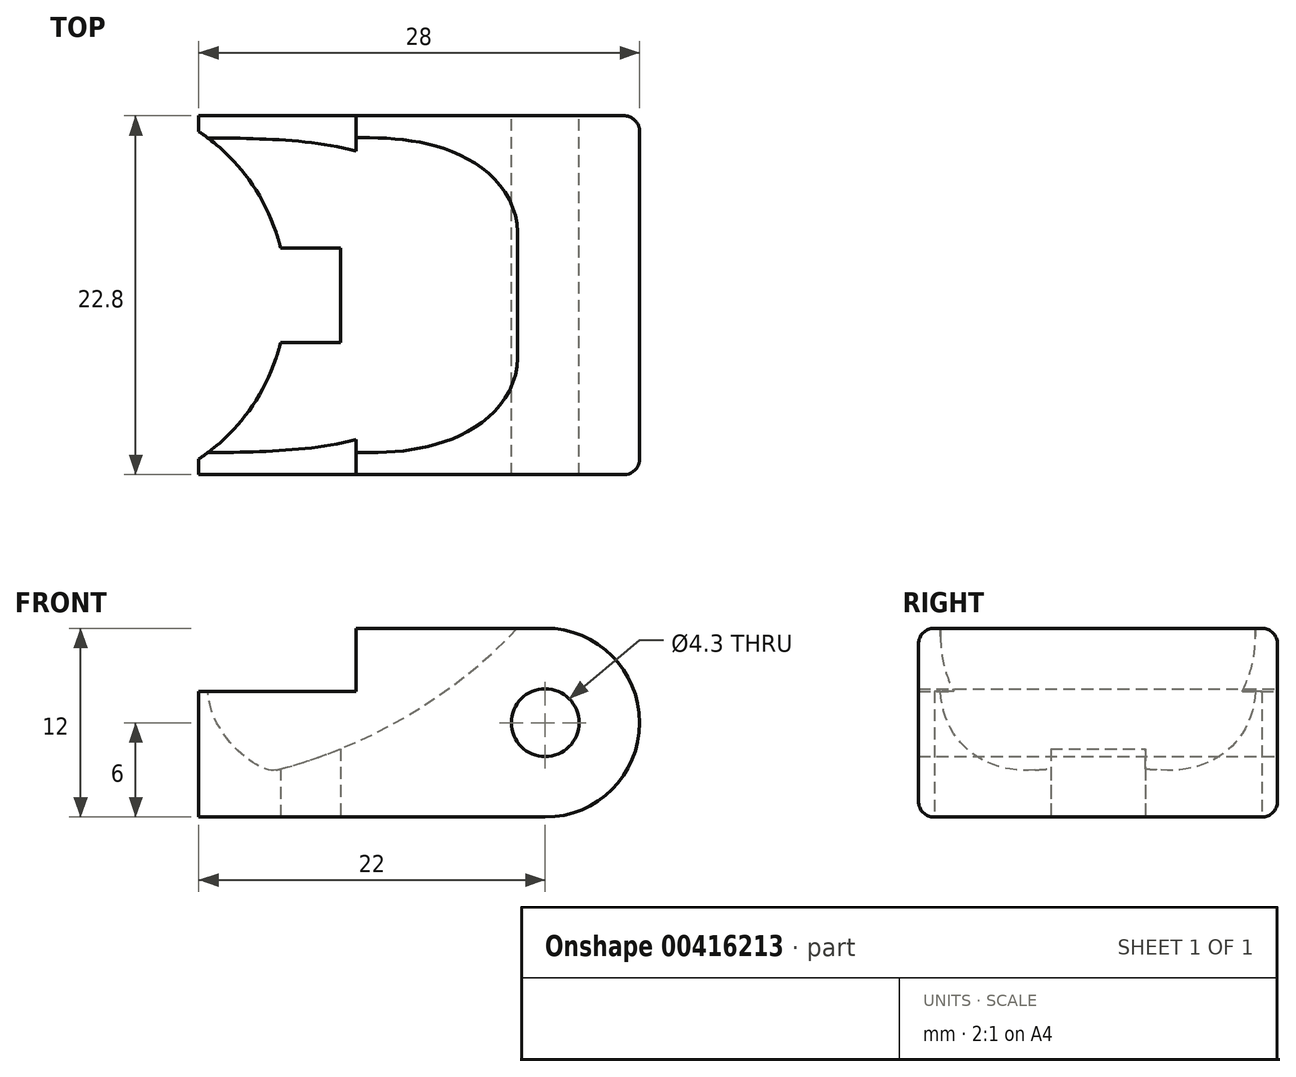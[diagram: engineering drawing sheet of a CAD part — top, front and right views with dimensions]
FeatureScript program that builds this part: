
annotation { "Feature Type Name" : "Feature", "Feature Type Description" : "" }
export const myFeature = defineFeature(function(context is Context, id is Id, definition is map)
    precondition{}
    {
        {
            var Q0;
            Q0=qCreatedBy(makeId("Front.planeOp"),FACE);
            var sketch = newSketch(context, id + "F0", { "sketchPlane" : qUnion([Q0])});
            skCircle(sketch, "E0", {"center": v(0, 0) * mm, "radius": 2.15 * mm});
            skArc(sketch, "E1", {"start": v(0, -6) * mm, "mid": v(6, 0) * mm, "end": v(0, 6) * mm});
            skLineSegment(sketch, "E2", {"start": v(0, 6) * mm, "end": v(-12, 6) * mm});
            skLineSegment(sketch, "E3", {"start": v(-12, 6) * mm, "end": v(-12, 2) * mm});
            skLineSegment(sketch, "E4", {"start": v(-12, 2) * mm, "end": v(-22, 2) * mm});
            skLineSegment(sketch, "E5", {"start": v(-22, 2) * mm, "end": v(-22, -6) * mm});
            skLineSegment(sketch, "E6", {"start": v(0, -6) * mm, "end": v(-22, -6) * mm});
            skSolve(sketch);
        }
        {
            var Q0;
            Q0 = qSketchRegion(id + "F0", true);
            extrude(context, id + "F1", {"entities" : qUnion([Q0]), "endBound" : BoundingType.SYMMETRIC, "depth" : 22.8 * mm});
        }
        {
            var Q0;
            Q0=qCreatedBy(makeId("Front.planeOp"),FACE);
            var sketch = newSketch(context, id + "F2", { "sketchPlane" : qUnion([Q0])});
            skArc(sketch, "E7", {"start": v(-26.32, -3.97) * mm, "mid": v(-10.73, -0.64) * mm, "end": v(1.32, 9.8) * mm});
            skLineSegment(sketch, "E8", {"start": v(-26.32, -3.97) * mm, "end": v(-26.32, 9.8) * mm});
            skLineSegment(sketch, "E9", {"start": v(-26.32, 9.8) * mm, "end": v(1.32, 9.8) * mm});
            skSolve(sketch);
        }
        {
            var Q0;
            Q0 = qSketchRegion(id + "F2", true);
            extrude(context, id + "F3", {"entities" : qUnion([Q0]), "operationType" : NewBodyOperationType.REMOVE, "endBound" : BoundingType.SYMMETRIC, "depth" : 20 * mm});
        }
        {
            var Q0;
            Q0=makeQuery(id+"F3.boolean.opBoolean","COPY",EDGE,{"derivedFrom":makeQuery(id+"F3.opExtrude","CAP_EDGE",EDGE,{"disambiguationData":[OSD([sQuery(id+"F2.wireOp",EDGE,"E7")])],"isStart":true})});
            var Q1;
            Q1=makeQuery(id+"F3.boolean.opBoolean","COPY",EDGE,{"derivedFrom":makeQuery(id+"F3.opExtrude","CAP_EDGE",EDGE,{"disambiguationData":[OSD([sQuery(id+"F2.wireOp",EDGE,"E7")])],"isStart":false})});
            fillet(context, id + "F4", {"entities" : qUnion([Q0, Q1]), "radius" : 6 * mm, "tangentPropagation" : true, "allowEdgeOverflow" : false});
        }
        {
            var Q0;
            Q0=makeQuery(id+"F1.opExtrude","SWEPT_FACE",FACE,{"disambiguationData":[OSD([sQuery(id+"F0.wireOp",EDGE,"E6")])]});
            var sketch = newSketch(context, id + "F5", { "sketchPlane" : qUnion([Q0])});
            skLineSegment(sketch, "E10", {"start": v(-16.8, 3) * mm, "end": v(-13, 3) * mm});
            skLineSegment(sketch, "E11", {"start": v(-13, 3) * mm, "end": v(-13, -3) * mm});
            skLineSegment(sketch, "E12", {"start": v(-13, -3) * mm, "end": v(-16.8, -3) * mm});
            skArc(sketch, "E13", {"start": v(-22, -10.4) * mm, "mid": v(-18.7, -7.19) * mm, "end": v(-16.8, -3) * mm});
            skArc(sketch, "E14.trimOffspring", {"start": v(-16.8, 3) * mm, "mid": v(-18.7, 7.19) * mm, "end": v(-22, 10.4) * mm});
            skLineSegment(sketch, "E15", {"start": v(-22, 10.4) * mm, "end": v(-22, -10.4) * mm});
            skSolve(sketch);
        }
        {
            var Q0;
            Q0=makeQuery(id+"F5.imprint","IMPRINT",FACE,{"disambiguationData":[TD([[makeQuery(id+"F5.imprint","IMPRINT",EDGE,{"derivedFrom":sQuery(id+"F5.wireOp",EDGE,"E10")}),-1.0]])]});
            extrude(context, id + "F6", {"entities" : qUnion([Q0]), "operationType" : NewBodyOperationType.REMOVE, "oppositeDirection" : true, "depth" : 25 * mm});
        }
        {
            var Q0;
            Q0=makeQuery(id+"F1.opExtrude","CAP_EDGE",EDGE,{"disambiguationData":[OSD([sQuery(id+"F0.wireOp",EDGE,"E2")])],"isStart":false});
            var Q1;
            Q1=makeQuery(id+"F1.opExtrude","CAP_EDGE",EDGE,{"disambiguationData":[OSD([sQuery(id+"F0.wireOp",EDGE,"E6")])],"isStart":true});
            fillet(context, id + "F7", {"entities" : qUnion([Q0, Q1]), "radius" : 1 * mm, "tangentPropagation" : true, "allowEdgeOverflow" : false});
        }
    });
